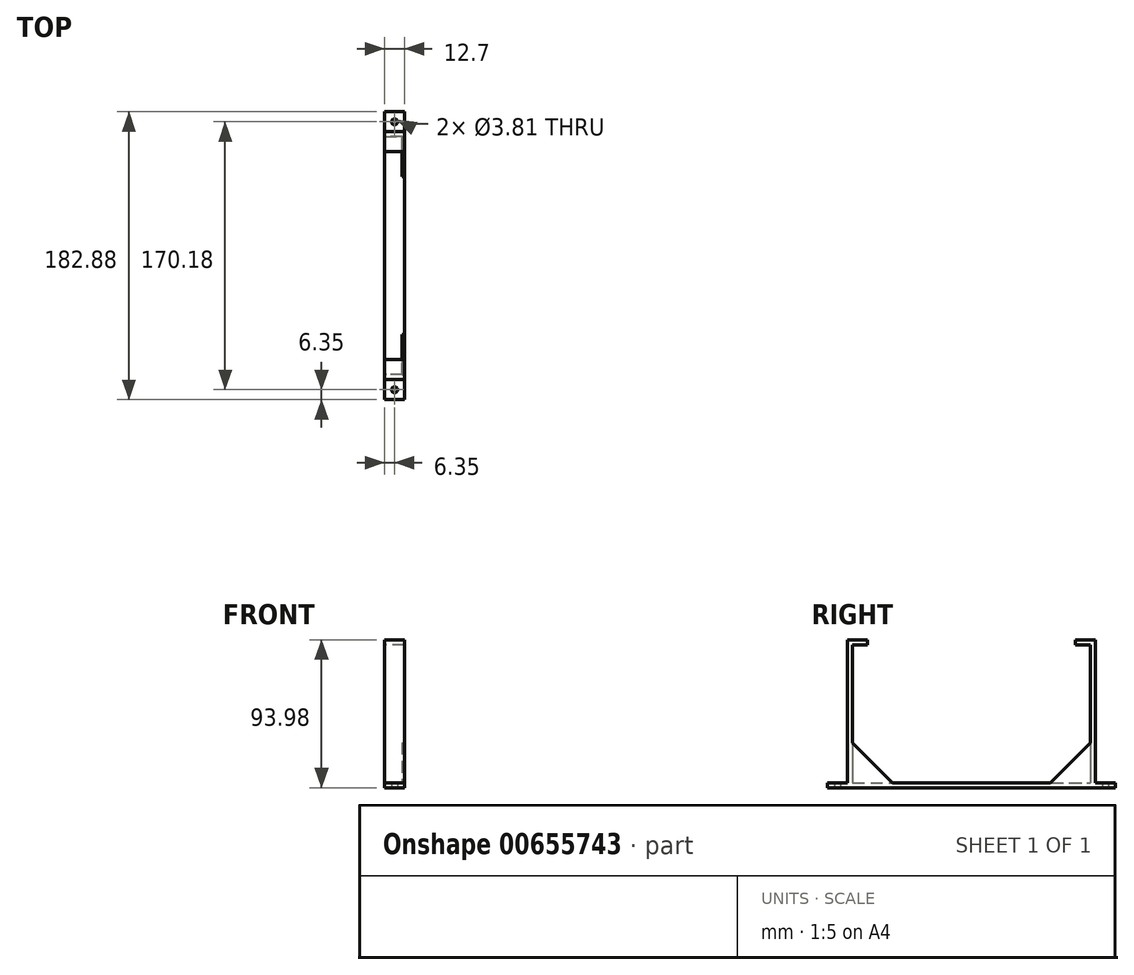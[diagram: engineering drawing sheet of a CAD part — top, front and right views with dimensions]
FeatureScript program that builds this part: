
annotation { "Feature Type Name" : "Feature", "Feature Type Description" : "" }
export const myFeature = defineFeature(function(context is Context, id is Id, definition is map)
    precondition{}
    {
        {
            var Q0;
            Q0=qCreatedBy(makeId("Top.planeOp"),FACE);
            var sketch = newSketch(context, id + "F0", { "sketchPlane" : qUnion([Q0])});
            skLineSegment(sketch, "E0.bottom", {"start": v(6.35, -75.57) * mm, "end": v(-6.35, -75.57) * mm});
            skLineSegment(sketch, "E0.top", {"start": v(6.35, 75.57) * mm, "end": v(-6.35, 75.57) * mm});
            skLineSegment(sketch, "E0.left", {"start": v(6.35, -75.57) * mm, "end": v(6.35, 75.57) * mm});
            skLineSegment(sketch, "E0.right", {"start": v(-6.35, -75.57) * mm, "end": v(-6.35, 75.57) * mm});
            skPoint(sketch, "E0.middle", {"position": v(0, 0) * mm});
            skLineSegment(sketch, "E1.bottom", {"start": v(6.35, -91.44) * mm, "end": v(-6.35, -91.44) * mm});
            skLineSegment(sketch, "E1.top", {"start": v(6.35, 91.44) * mm, "end": v(-6.35, 91.44) * mm});
            skLineSegment(sketch, "E1.left", {"start": v(6.35, -91.44) * mm, "end": v(6.35, 91.44) * mm});
            skLineSegment(sketch, "E1.right", {"start": v(-6.35, -91.44) * mm, "end": v(-6.35, 91.44) * mm});
            skLineSegment(sketch, "E2.bottom", {"start": v(6.35, -78.74) * mm, "end": v(-6.35, -78.74) * mm});
            skLineSegment(sketch, "E2.top", {"start": v(6.35, 78.74) * mm, "end": v(-6.35, 78.74) * mm});
            skLineSegment(sketch, "E2.left", {"start": v(6.35, -78.74) * mm, "end": v(6.35, 78.74) * mm});
            skLineSegment(sketch, "E2.right", {"start": v(-6.35, -78.74) * mm, "end": v(-6.35, 78.74) * mm});
            skCircle(sketch, "E3", {"center": v(0, 85.1) * mm, "radius": 1.9 * mm});
            skPoint(sketch, "E3.centerSnap0", {"position": v(0, 78.74) * mm});
            skCircle(sketch, "E4.MirrorC", {"center": v(0, -85.1) * mm, "radius": 1.9 * mm});
            skSolve(sketch);
        }
        {
            var Q0;
            {var subQ0=sQuery(id+"F0.wireOp",EDGE,"E0.bottom");Q0=makeQuery(id+"F0.imprint","IMPRINT",FACE,{"disambiguationData":[TD([[makeQuery(id+"F0.imprint","IMPRINT",EDGE,{"derivedFrom":subQ0}),-1.0]])]});}
            extrude(context, id + "F1", {"entities" : qUnion([Q0]), "depth" : 3.17 * mm, "offsetDistance" : 25.4 * mm});
        }
        {
            var Q0;
            {var subQ0=sQuery(id+"F0.wireOp",EDGE,"E0.top");Q0=makeQuery(id+"F0.imprint","IMPRINT",FACE,{"disambiguationData":[TD([[makeQuery(id+"F0.imprint","IMPRINT",EDGE,{"derivedFrom":subQ0}),-1.0]])]});}
            var Q1;
            {var subQ0=sQuery(id+"F0.wireOp",EDGE,"E0.bottom");Q1=makeQuery(id+"F0.imprint","IMPRINT",FACE,{"disambiguationData":[TD([[makeQuery(id+"F0.imprint","IMPRINT",EDGE,{"derivedFrom":subQ0}),1.0]])]});}
            extrude(context, id + "F2", {"entities" : qUnion([Q0, Q1]), "operationType" : NewBodyOperationType.ADD, "depth" : 93.98 * mm, "offsetDistance" : 25.4 * mm});
        }
        {
            var Q0;
            {var subQ2=sQuery(id+"F0.wireOp",EDGE,"E1.top");Q0=makeQuery(id+"F0.imprint","IMPRINT",FACE,{"disambiguationData":[TD([[makeQuery(id+"F0.imprint","IMPRINT",EDGE,{"derivedFrom":subQ2}),1.0]])]});}
            var Q1;
            {var subQ2=sQuery(id+"F0.wireOp",EDGE,"E1.bottom");Q1=makeQuery(id+"F0.imprint","IMPRINT",FACE,{"disambiguationData":[TD([[makeQuery(id+"F0.imprint","IMPRINT",EDGE,{"derivedFrom":subQ2}),-1.0]])]});}
            extrude(context, id + "F3", {"entities" : qUnion([Q0, Q1]), "operationType" : NewBodyOperationType.ADD, "depth" : 3.17 * mm, "offsetDistance" : 25.4 * mm});
        }
        {
            var Q0;
            Q0=makeQuery(id+"F2.opExtrude","SWEPT_FACE",FACE,{"disambiguationData":[OSD([sQuery(id+"F0.wireOp",EDGE,"E0.top")])]});
            var sketch = newSketch(context, id + "F4", { "sketchPlane" : qUnion([Q0])});
            skLineSegment(sketch, "E5.bottom", {"start": v(-6.35, 93.98) * mm, "end": v(6.35, 93.98) * mm});
            skLineSegment(sketch, "E5.top", {"start": v(-6.35, 90.8) * mm, "end": v(6.35, 90.8) * mm});
            skLineSegment(sketch, "E5.left", {"start": v(-6.35, 93.98) * mm, "end": v(-6.35, 90.8) * mm});
            skLineSegment(sketch, "E5.right", {"start": v(6.35, 93.98) * mm, "end": v(6.35, 90.8) * mm});
            skSolve(sketch);
        }
        {
            var Q0;
            Q0=makeQuery(id+"F4.imprint","IMPRINT",FACE,{"disambiguationData":[TD([[makeQuery(id+"F4.imprint","IMPRINT",EDGE,{"derivedFrom":sQuery(id+"F4.wireOp",EDGE,"E5.bottom")}),1.0]])]});
            extrude(context, id + "F5", {"entities" : qUnion([Q0]), "operationType" : NewBodyOperationType.ADD, "depth" : 9.52 * mm, "offsetDistance" : 25.4 * mm});
        }
        {
            var Q0;
            Q0=makeQuery(id+"F2.opExtrude","SWEPT_FACE",FACE,{"disambiguationData":[OSD([sQuery(id+"F0.wireOp",EDGE,"E0.bottom")])]});
            var sketch = newSketch(context, id + "F6", { "sketchPlane" : qUnion([Q0])});
            skLineSegment(sketch, "E6.bottom", {"start": v(-6.35, 93.98) * mm, "end": v(6.35, 93.98) * mm});
            skLineSegment(sketch, "E6.top", {"start": v(-6.35, 90.8) * mm, "end": v(6.35, 90.8) * mm});
            skLineSegment(sketch, "E6.left", {"start": v(-6.35, 93.98) * mm, "end": v(-6.35, 90.8) * mm});
            skLineSegment(sketch, "E6.right", {"start": v(6.35, 93.98) * mm, "end": v(6.35, 90.8) * mm});
            skSolve(sketch);
        }
        {
            var Q0;
            Q0=makeQuery(id+"F6.imprint","IMPRINT",FACE,{"disambiguationData":[TD([[makeQuery(id+"F6.imprint","IMPRINT",EDGE,{"derivedFrom":sQuery(id+"F6.wireOp",EDGE,"E6.bottom")}),-1.0]])]});
            extrude(context, id + "F7", {"entities" : qUnion([Q0]), "operationType" : NewBodyOperationType.ADD, "depth" : 9.52 * mm, "offsetDistance" : 25.4 * mm});
        }
        {
            var Q0;
            {var subQ0=sQuery(id+"F0.wireOp",EDGE,"E1.left");var subQ1=sQuery(id+"F0.wireOp",EDGE,"E2.left");Q0=makeQuery(id+"F7.boolean.opBoolean","MERGE",FACE,{"derivedFrom":[makeQuery(id+"F5.boolean.opBoolean","MERGE",FACE,{"derivedFrom":[makeQuery(id+"F3.boolean.opBoolean","MERGE",FACE,{"derivedFrom":[makeQuery(id+"F2.boolean.opBoolean","MERGE",FACE,{"derivedFrom":[makeQuery(id+"F1.opExtrude","SWEPT_FACE",FACE,{"disambiguationData":[OSD([subQ1])]}),makeQuery(id+"F2.opExtrude","SWEPT_FACE",FACE,{"disambiguationData":[OSD([subQ1]),TDD([makeQuery(id+"F0.imprint","IMPRINT",EDGE,{"disambiguationData":[TD([[makeQuery(id+"F0.imprint","INTERSECT",VERTEX,{"derivedFrom":[sQuery(id+"F0.wireOp",EDGE,"E0.bottom"),subQ1]}),1.0]])],"derivedFrom":subQ1})])]}),makeQuery(id+"F2.opExtrude","SWEPT_FACE",FACE,{"disambiguationData":[OSD([subQ1]),TDD([makeQuery(id+"F0.imprint","IMPRINT",EDGE,{"disambiguationData":[TD([[makeQuery(id+"F0.imprint","INTERSECT",VERTEX,{"derivedFrom":[sQuery(id+"F0.wireOp",EDGE,"E0.top"),subQ1]}),-1.0]])],"derivedFrom":subQ1})])]})]}),makeQuery(id+"F3.opExtrude","SWEPT_FACE",FACE,{"disambiguationData":[OSD([subQ0]),TDD([makeQuery(id+"F0.imprint","IMPRINT",EDGE,{"disambiguationData":[TD([[makeQuery(id+"F0.imprint","INTERSECT",VERTEX,{"derivedFrom":[sQuery(id+"F0.wireOp",EDGE,"E1.bottom"),subQ0]}),-1.0]])],"derivedFrom":subQ0})])]}),makeQuery(id+"F3.opExtrude","SWEPT_FACE",FACE,{"disambiguationData":[OSD([subQ0]),TDD([makeQuery(id+"F0.imprint","IMPRINT",EDGE,{"disambiguationData":[TD([[makeQuery(id+"F0.imprint","INTERSECT",VERTEX,{"derivedFrom":[sQuery(id+"F0.wireOp",EDGE,"E1.top"),subQ0]}),1.0]])],"derivedFrom":subQ0})])]})]}),makeQuery(id+"F5.opExtrude","SWEPT_FACE",FACE,{"disambiguationData":[OSD([sQuery(id+"F4.wireOp",EDGE,"E5.right")])]})]}),makeQuery(id+"F7.opExtrude","SWEPT_FACE",FACE,{"disambiguationData":[OSD([sQuery(id+"F6.wireOp",EDGE,"E6.left")])]})]});}
            var sketch = newSketch(context, id + "F8", { "sketchPlane" : qUnion([Q0])});
            skLineSegment(sketch, "E7", {"start": v(50.16, 3.17) * mm, "end": v(75.57, 28.57) * mm});
            skLineSegment(sketch, "E8.MirrorCS", {"start": v(-50.16, 3.17) * mm, "end": v(-75.57, 28.58) * mm});
            skSolve(sketch);
        }
        {
            var Q0;
            {var subQ0=sQuery(id+"F8.wireOp",EDGE,"E7");Q0=makeQuery(id+"F8.imprint","IMPRINT",FACE,{"disambiguationData":[TD([[makeQuery(id+"F8.imprint","IMPRINT",EDGE,{"derivedFrom":subQ0}),-1.0]])]});}
            var Q1;
            {var subQ0=sQuery(id+"F8.wireOp",EDGE,"E8.MirrorCS");Q1=makeQuery(id+"F8.imprint","IMPRINT",FACE,{"disambiguationData":[TD([[makeQuery(id+"F8.imprint","IMPRINT",EDGE,{"derivedFrom":subQ0}),1.0]])]});}
            extrude(context, id + "F9", {"entities" : qUnion([Q0, Q1]), "operationType" : NewBodyOperationType.ADD, "oppositeDirection" : true, "depth" : 1.56 * mm, "offsetDistance" : 25.4 * mm});
        }
    });
